# Revit family: equip-sink-elkay-scrub-wall-acm
name_source: partatom
category: Plumbing Fixtures
units: mm (PartAtom-declared; Revit-internal decimal feet)

## family parameters
Cut with Voids When Loaded = No
Host = Face
Part Type = Normal
Room Calculation Point = No
Round Connector Dimension = Use Radius
Shared = No

## types (8) — shared parameters
Assembly Code = D2010410
Backsplash Height = 0' - 6"
Backsplash Width = 0' - 2"
Backsplash Width Hidden = 0' - 2"
Bowl Depth = 0' - 10 1/2"
Bowl Drain Location FB = 0' - 8"
Bowl Width = 1' - 4"
Bubbler CW Flow Rate = 2 GPM
Bubbler Material = Metal - Steel - Stainless - Chrome
Bubbler Nominal Dia = 0' - 0 1/2"
Bubbler Nominal Radius = 0' - 0 1/4"
CW Flow Rate = 2 GPM
Cost = 1 $
Default Elevation = 3' - 0"
Description = Wash-Up Lavatory Sinks
Drain Material = Metal - Steel - Stainless - Chrome
Faucet CL Horiz to Control Box Outlet = 0' - 2 5/8"
Faucet CL from Top Backsplash = 0' - 2 1/2"
Faucet Hole Dia = 0' - 1 1/4"
Faucet Hole One = Yes
Faucet Hole One Top = 0' - 0 1/4"
Faucet Hole One to CL = 0' - 0"
Faucet Hole Two = No
Faucet Hole Two Top = 0' - 0 1/8"
Faucet Material = Metal - Steel - Stainless - Chrome
Faucet Part = LKB722C
Faucet Water Supply Radius = 0' - 0 3/16"
HW Flow Rate = 2 GPM
Hidden Width = 1' - 7 1/2"
Hole One to Two = 0' - 4"
Hole Radius = 0' - 0 5/8"
Keynote = D2010410
Manufacturer = Elkay Manufacturing
MasterFormat Number = 22.42.16.16
MasterFormat Title = Commercial Sinks
Nominal Dia = 0' - 0 1/2"
Nominal Radius = 0' - 0 1/4"
OmniClass Code = 23.45.05.14.14.27
OmniClass Title = Service Sinks
Reference Level to Back Plane = 0' - 0"
Rough-In Sanitary Installation Height = 1' - 9"
Rough-In Sanitary Right From CL Sink = 0' - 2"
Rough-In Water Supply Distance Left from CL Sink = 0' - 1 1/8"
Rough-In Water Supply Installation Height = 0' - 8 5/8"
Sanitary Flow Rate = 10 GPM
Sanitary Nominal Dia = 0' - 1 1/2"
Sanitary Nominal Radius = 0' - 0 3/4"
Sink Material = Metal - Steel - Stainless - Chrome
Sink Rim Front Width = 0' - 1 1/2"
Sink Rim Front Width Hidden = 0' - 1 1/2"
Sink Rim Left Width = 0' - 1 1/2"
Sink Rim Left Width Hidden = 0' - 1 1/2"
Sink Rim Right Width = 0' - 1 1/2"
Sink Rim Right Width Hidden = 0' - 1 1/2"
Sink San Conn Extr Visibility = No
Sink Width = 1' - 7 1/2"
Specification Sheet URL = http://www.elkayusa.com
Stem Material = Metal - Steel
Thermostatic Mix Valve = No
URL = www.elkayusa.com
Valve Material = Metal - Steel - Stainless - Chrome
Vent Connection = Yes
zero-valued in all types: CWFU, HWFU, WFU

## per-type parameters (varying)
| type | AC Power | Bowl Length | Drain CL LR to Left Bowl Edge | Hidden Length | Mechanical Mix Valve | Mix Valve Part | No Mix Valve | Sink Length | Sink Part | Supply Line Mix Length |
| EWS2520SACC | Yes | 1' - 10" | 0' - 11" | 2' - 1" | No |  | Yes | 2' - 1" | EWS25201 | 0' - 2" |
| EWS2520SACMC | Yes | 1' - 10" | 0' - 11" | 2' - 1" | Yes | LK724 | No | 2' - 1" | EWS25201 | 0' - 0 1/2" |
| EWS2520SBMC | No | 1' - 10" | 0' - 11" | 2' - 1" | Yes | LK724 | No | 2' - 1" | EWS25201 | 0' - 0 1/2" |
| EWS2520SBC | No | 1' - 10" | 0' - 11" | 2' - 1" | No |  | Yes | 2' - 1" | EWS25201 | 0' - 2" |
| EWS3120SACC | Yes | 2' - 4" | 1' - 2" | 2' - 7" | No |  | Yes | 2' - 7" | EWS31201 | 0' - 2" |
| EWS3120SACMC | Yes | 2' - 4" | 1' - 2" | 2' - 7" | Yes | LK724 | No | 2' - 7" | EWS31201 | 0' - 0 1/2" |
| EWS3120SBC | No | 2' - 4" | 1' - 2" | 2' - 7" | No |  | Yes | 2' - 7" | EWS31201 | 0' - 2" |
| EWS3120SBMC | No | 2' - 4" | 1' - 2" | 2' - 7" | Yes | LK724 | No | 2' - 7" | EWS31201 | 0' - 0 1/2" |

note: column(s) folded — value = type name in every type: Model

## geometry (parser evidence)
native form markers: Sweep x14
no freeform markers — native parametric forms only
